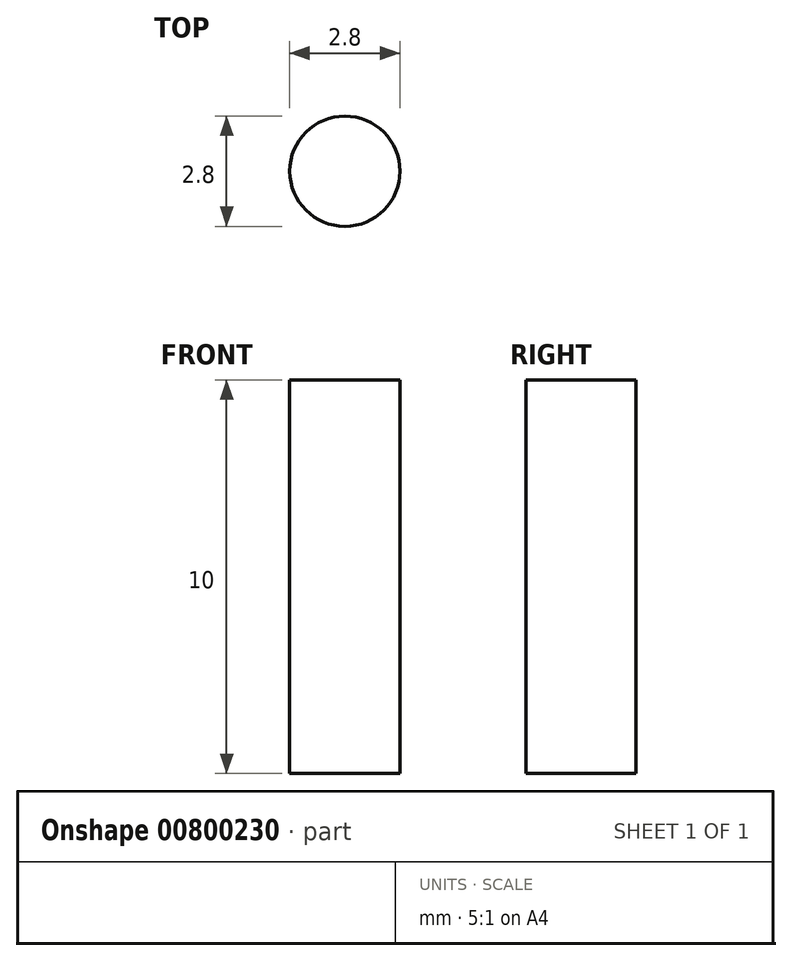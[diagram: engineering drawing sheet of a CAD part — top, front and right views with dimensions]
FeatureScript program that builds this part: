
annotation { "Feature Type Name" : "Feature", "Feature Type Description" : "" }
export const myFeature = defineFeature(function(context is Context, id is Id, definition is map)
    precondition{}
    {
        {
            var Q0;
            Q0=qCreatedBy(makeId("Top.planeOp"),FACE);
            var sketch = newSketch(context, id + "F0", { "sketchPlane" : qUnion([Q0])});
            skCircle(sketch, "E0", {"center": v(-14.06, 0) * mm, "radius": 1.4 * mm});
            skSolve(sketch);
        }
        {
            var Q0;
            Q0=makeQuery(id+"F0.imprint","IMPRINT",FACE,{"disambiguationData":[TD([[makeQuery(id+"F0.imprint","IMPRINT",EDGE,{"derivedFrom":sQuery(id+"F0.wireOp",EDGE,"E0")}),1.0]])]});
            extrude(context, id + "F1", {"entities" : qUnion([Q0]), "depth" : 10 * mm, "offsetDistance" : 25 * mm});
        }
    });
